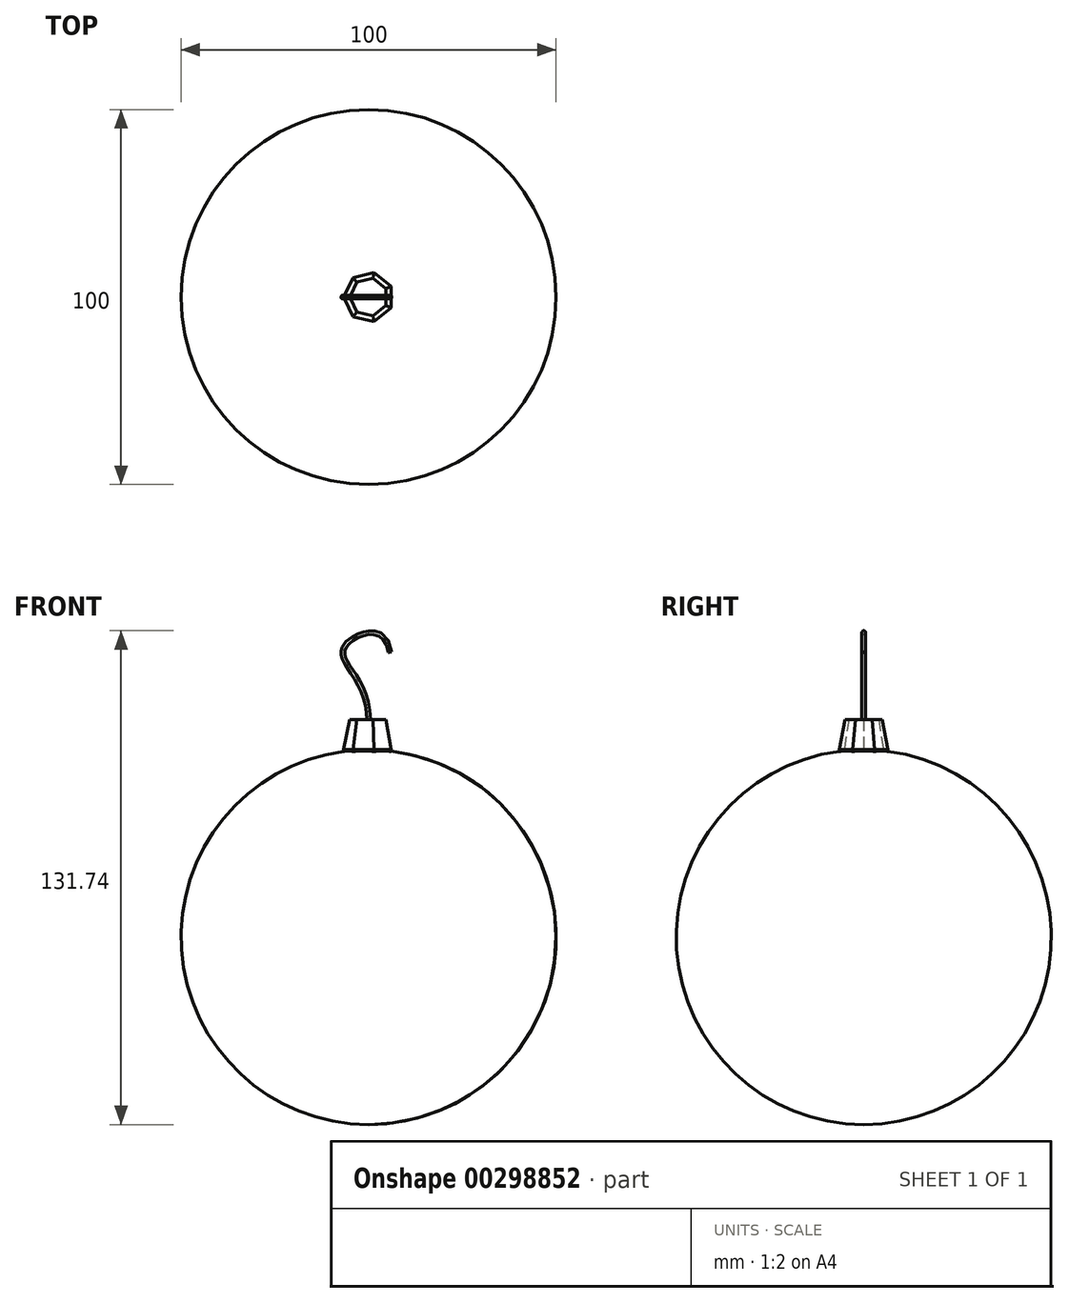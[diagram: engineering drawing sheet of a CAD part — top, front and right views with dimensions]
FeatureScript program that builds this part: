
annotation { "Feature Type Name" : "Feature", "Feature Type Description" : "" }
export const myFeature = defineFeature(function(context is Context, id is Id, definition is map)
    precondition{}
    {
        {
            var Q0;
            Q0=qCreatedBy(makeId("Front.planeOp"),FACE);
            var sketch = newSketch(context, id + "F0", { "sketchPlane" : qUnion([Q0])});
            skArc(sketch, "E0", {"start": v(0, 50) * mm, "mid": v(-50, 0) * mm, "end": v(0, -50) * mm});
            skLineSegment(sketch, "E1", {"start": v(0, 50) * mm, "end": v(0, -50) * mm});
            skSolve(sketch);
        }
        {
            var Q0;
            Q0 = qSketchRegion(id + "F0", true);
            var Q1;
            Q1 = qConstructionFilter(qBodyType(qCreatedBy(id + "F0" ,EDGE), BodyType.WIRE), ConstructionObject.NO);
            var Q2;
            Q2=sQuery(id+"F0.wireOp",EDGE,"E1");
            revolve(context, id + "F1", {"surfaceOperationType" : NewSurfaceOperationType.NEW, "entities" : qUnion([Q0]), "surfaceEntities" : qUnion([Q1]), "axis" : qUnion([Q2]), "revolveType" : RevolveType.FULL});
        }
        {
            var Q0;
            Q0=sQuery(id+"F0.wireOp",VERTEX,"E0.start");
            var Q1;
            Q1=sQuery(id+"F0.wireOp",EDGE,"E1");
            cPlane(context, id + "F2", {"entities" : qUnion([Q0, Q1]), "cplaneType" : CPlaneType.LINE_POINT, "offset" : 25 * mm, "width" : 150 * mm, "height" : 150 * mm});
        }
        {
            var Q0;
            Q0=qCreatedBy(id+"F2.planeOp",FACE);
            var sketch = newSketch(context, id + "F3", { "sketchPlane" : qUnion([Q0])});
            skCircle(sketch, "E2.cCircle", {"center": v(0, 0) * mm, "radius": 6 * mm, "construction": true});
            skLineSegment(sketch, "E2.0", {"start": v(6, 2.89) * mm, "end": v(6, -2.89) * mm});
            skLineSegment(sketch, "E2.1", {"start": v(6, -2.89) * mm, "end": v(1.48, -6.5) * mm});
            skLineSegment(sketch, "E2.2", {"start": v(1.48, -6.5) * mm, "end": v(-4.15, -5.2) * mm});
            skLineSegment(sketch, "E2.3", {"start": v(-4.15, -5.2) * mm, "end": v(-6.66, 0) * mm});
            skLineSegment(sketch, "E2.4", {"start": v(-6.66, 0) * mm, "end": v(-4.15, 5.2) * mm});
            skLineSegment(sketch, "E2.5", {"start": v(-4.15, 5.2) * mm, "end": v(1.48, 6.5) * mm});
            skLineSegment(sketch, "E2.6", {"start": v(1.48, 6.5) * mm, "end": v(6, 2.89) * mm});
            skPoint(sketch, "E2.0.midPoint", {"position": v(6, 0) * mm});
            skSolve(sketch);
        }
        {
            var Q0;
            Q0 = qSketchRegion(id + "F3", true);
            extrude(context, id + "F4", {"entities" : qUnion([Q0]), "oppositeDirection" : true, "depth" : 8 * mm, "offsetDistance" : 25 * mm, "hasDraft" : true, "draftAngle" : 10 * degree, "draftPullDirection" : true});
        }
        {
            var Q0;
            Q0=makeQuery(id+"F4.opExtrude","CAP_FACE",FACE,{"disambiguationData":[OSD([sQuery(id+"F3.wireOp",EDGE,"E2.0"),sQuery(id+"F3.wireOp",EDGE,"E2.1"),sQuery(id+"F3.wireOp",EDGE,"E2.2"),sQuery(id+"F3.wireOp",EDGE,"E2.3"),sQuery(id+"F3.wireOp",EDGE,"E2.4"),sQuery(id+"F3.wireOp",EDGE,"E2.5"),sQuery(id+"F3.wireOp",EDGE,"E2.6")])],"isStart":true});
            extrude(context, id + "F5", {"entities" : qUnion([Q0]), "operationType" : NewBodyOperationType.ADD, "endBound" : BoundingType.UP_TO_NEXT, "depth" : 25 * mm, "offsetDistance" : 25 * mm});
        }
        {
            var Q0;
            Q0=qCreatedBy(makeId("Front.planeOp"),FACE);
            var sketch = newSketch(context, id + "F6", { "sketchPlane" : qUnion([Q0])});
            skLineSegment(sketch, "E3.0.4", {"start": v(-5.1, 58) * mm, "end": v(-3.18, 58) * mm, "construction": true});
            skPoint(sketch, "E4", {"position": v(0, 58) * mm});
            skFitSpline(sketch, "E5", {"points": [v(0, 58) * mm, v(-6.4, 77.55) * mm, v(5.69, 76.02) * mm], "startDerivative": vector(0, 59.48) * mm, "endDerivative": vector(7.38, -58.2) * mm});
            skSolve(sketch);
        }
        {
            var Q0;
            Q0=makeQuery(id+"F4.opExtrude","CAP_FACE",FACE,{"disambiguationData":[OSD([sQuery(id+"F3.wireOp",EDGE,"E2.0"),sQuery(id+"F3.wireOp",EDGE,"E2.1"),sQuery(id+"F3.wireOp",EDGE,"E2.2"),sQuery(id+"F3.wireOp",EDGE,"E2.3"),sQuery(id+"F3.wireOp",EDGE,"E2.4"),sQuery(id+"F3.wireOp",EDGE,"E2.5"),sQuery(id+"F3.wireOp",EDGE,"E2.6")])],"isStart":false});
            var sketch = newSketch(context, id + "F7", { "sketchPlane" : qUnion([Q0])});
            skCircle(sketch, "E6", {"center": v(0, 0) * mm, "radius": 0.5 * mm});
            skSolve(sketch);
        }
        {
            var Q0;
            Q0=makeQuery(id+"F7.imprint","IMPRINT",FACE,{"disambiguationData":[TD([[makeQuery(id+"F7.imprint","IMPRINT",EDGE,{"derivedFrom":sQuery(id+"F7.wireOp",EDGE,"E6")}),1.0]])]});
            var Q1;
            Q1=sQuery(id+"F6.wireOp",EDGE,"E5");
            sweep(context, id + "F8", {"profiles" : qUnion([Q0]), "path" : qUnion([Q1])});
        }
    });
